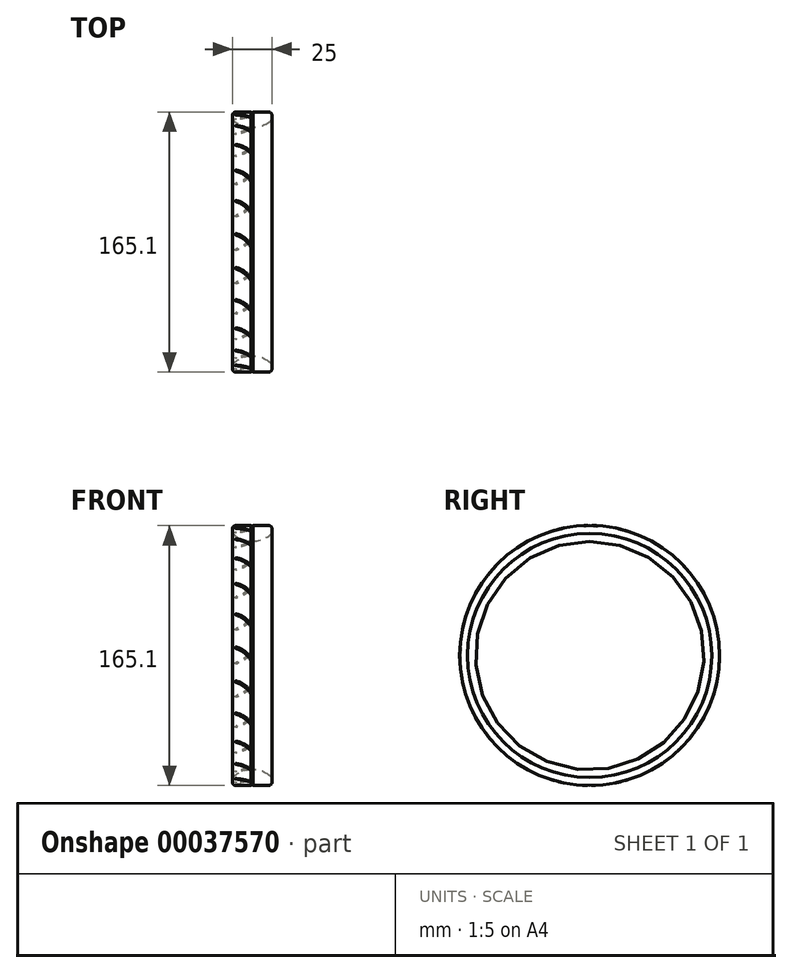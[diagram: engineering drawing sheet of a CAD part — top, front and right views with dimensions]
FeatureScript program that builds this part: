
annotation { "Feature Type Name" : "Feature", "Feature Type Description" : "" }
export const myFeature = defineFeature(function(context is Context, id is Id, definition is map)
    precondition{}
    {
        {
            var Q0;
            Q0=qCreatedBy(makeId("Top.planeOp"),FACE);
            var sketch = newSketch(context, id + "F0", { "sketchPlane" : qUnion([Q0])});
            skLineSegment(sketch, "E0", {"start": v(-134.1, 0) * mm, "end": v(143.87, 0) * mm, "construction": true});
            skLineSegment(sketch, "E1.left", {"start": v(-12.5, 80.55) * mm, "end": v(-12.5, 77.55) * mm});
            skLineSegment(sketch, "E1.right", {"start": v(12.5, 80.55) * mm, "end": v(12.5, 77.55) * mm});
            skArc(sketch, "E2", {"start": v(-12.5, 77.55) * mm, "mid": v(0, 72.59) * mm, "end": v(12.5, 77.55) * mm});
            skLineSegment(sketch, "E3", {"start": v(-10.5, 82.55) * mm, "end": v(-0.6, 82.55) * mm});
            skPoint(sketch, "E4.visualSharp", {"position": v(-12.5, 82.55) * mm});
            skArc(sketch, "E4.filletArc", {"start": v(-10.5, 82.55) * mm, "mid": v(-11.91, 81.96) * mm, "end": v(-12.5, 80.55) * mm});
            skPoint(sketch, "E5.visualSharp", {"position": v(12.5, 82.55) * mm});
            skArc(sketch, "E5.filletArc", {"start": v(12.5, 80.55) * mm, "mid": v(11.91, 81.96) * mm, "end": v(10.5, 82.55) * mm});
            skLineSegment(sketch, "E6.rect.bottom", {"start": v(0.6, 82.15) * mm, "end": v(-0.6, 82.15) * mm});
            skLineSegment(sketch, "E6.rect.left", {"start": v(0.6, 82.15) * mm, "end": v(0.6, 82.55) * mm});
            skLineSegment(sketch, "E6.rect.right", {"start": v(-0.6, 82.15) * mm, "end": v(-0.6, 82.55) * mm});
            skLineSegment(sketch, "E7.trimOffspring", {"start": v(0.6, 82.55) * mm, "end": v(10.5, 82.55) * mm});
            skSolve(sketch);
        }
        {
            var Q0;
            Q0=makeQuery(id+"F0.imprint","IMPRINT",FACE,{"disambiguationData":[TD([[makeQuery(id+"F0.imprint","IMPRINT",EDGE,{"derivedFrom":sQuery(id+"F0.wireOp",EDGE,"E1.left")}),1.0]])]});
            var Q1;
            Q1=sQuery(id+"F0.wireOp",EDGE,"E0");
            revolve(context, id + "F1", {"entities" : qUnion([Q0]), "axis" : qUnion([Q1]), "revolveType" : RevolveType.FULL});
        }
        {
            var Q0;
            Q0=qCreatedBy(makeId("Top.planeOp"),FACE);
            cPlane(context, id + "F2", {"entities" : qUnion([Q0]), "cplaneType" : CPlaneType.OFFSET, "offset" : 89.1 * mm, "width" : 150 * mm, "height" : 150 * mm});
        }
        {
            var Q0;
            Q0=qCreatedBy(makeId("Top.planeOp"),FACE);
            var sketch = newSketch(context, id + "F3", { "sketchPlane" : qUnion([Q0])});
            skLineSegment(sketch, "E8", {"start": v(-88.22, 0) * mm, "end": v(82.6, 0) * mm, "construction": true});
            skSolve(sketch);
        }
        {
            var Q0;
            Q0=qCreatedBy(id+"F2.planeOp",FACE);
            var sketch = newSketch(context, id + "F4", { "sketchPlane" : qUnion([Q0])});
            skArc(sketch, "E9", {"start": v(0, -5.08) * mm, "mid": v(-3.64, 1.64) * mm, "end": v(-10.3, 5.36) * mm});
            skArc(sketch, "E10", {"start": v(0, -5.08) * mm, "mid": v(-4.05, 0.87) * mm, "end": v(-10.3, 4.43) * mm});
            skArc(sketch, "E11", {"start": v(-10.3, 5.36) * mm, "mid": v(-10.68, 4.9) * mm, "end": v(-10.3, 4.43) * mm});
            skArc(sketch, "E12.MirrorCS", {"start": v(0, -5.08) * mm, "mid": v(3.64, 1.64) * mm, "end": v(10.3, 5.36) * mm});
            skArc(sketch, "E13.MirrorCS", {"start": v(0, -5.08) * mm, "mid": v(4.05, 0.87) * mm, "end": v(10.3, 4.43) * mm});
            skArc(sketch, "E14.MirrorCS", {"start": v(10.3, 5.36) * mm, "mid": v(10.68, 4.9) * mm, "end": v(10.3, 4.43) * mm});
            skSolve(sketch);
        }
        {
            var Q0;
            Q0=makeQuery(id+"F4.imprint","IMPRINT",FACE,{"disambiguationData":[TD([[makeQuery(id+"F4.imprint","IMPRINT",EDGE,{"derivedFrom":sQuery(id+"F4.wireOp",EDGE,"E9")}),1.0]])]});
            var Q1;
            Q1=makeQuery(id+"F4.imprint","IMPRINT",FACE,{"disambiguationData":[TD([[makeQuery(id+"F4.imprint","IMPRINT",EDGE,{"derivedFrom":sQuery(id+"F4.wireOp",EDGE,"E12.MirrorCS")}),-1.0]])]});
            var Q2;
            Q2=makeQuery(id+"F1.opRevolve","SWEPT_FACE",FACE,{"disambiguationData":[OSD([sQuery(id+"F0.wireOp",EDGE,"E6.rect.bottom")])]});
            extrude(context, id + "F5", {"entities" : qUnion([Q0, Q1]), "operationType" : NewBodyOperationType.REMOVE, "endBound" : BoundingType.UP_TO_SURFACE, "oppositeDirection" : true, "endBoundEntityFace" : qUnion([Q2]), "depth" : 1 * mm});
        }
        {
            var Q0;
            Q0=makeQuery(id+"F5.boolean.opBoolean","COPY",FACE,{"derivedFrom":makeQuery(id+"F5.opExtrude","SWEPT_FACE",FACE,{"disambiguationData":[OSD([sQuery(id+"F4.wireOp",EDGE,"E9")])]})});
            var Q1;
            Q1=makeQuery(id+"F5.boolean.opBoolean","COPY",FACE,{"derivedFrom":makeQuery(id+"F5.opExtrude","SWEPT_FACE",FACE,{"disambiguationData":[OSD([sQuery(id+"F4.wireOp",EDGE,"E11")])]})});
            var Q2;
            Q2=makeQuery(id+"F5.boolean.opBoolean","COPY",FACE,{"derivedFrom":makeQuery(id+"F5.opExtrude","SWEPT_FACE",FACE,{"disambiguationData":[OSD([sQuery(id+"F4.wireOp",EDGE,"E12.MirrorCS")])]})});
            var Q3;
            Q3=makeQuery(id+"F5.boolean.opBoolean","COPY",FACE,{"derivedFrom":makeQuery(id+"F5.opExtrude","SWEPT_FACE",FACE,{"disambiguationData":[OSD([sQuery(id+"F4.wireOp",EDGE,"E10")])]})});
            var Q4;
            Q4=makeQuery(id+"F5.boolean.opBoolean","COPY",FACE,{"derivedFrom":makeQuery(id+"F5.opExtrude","SWEPT_FACE",FACE,{"disambiguationData":[OSD([sQuery(id+"F4.wireOp",EDGE,"E13.MirrorCS")])]})});
            var Q5;
            Q5=makeQuery(id+"F5.boolean.opBoolean","COPY",FACE,{"derivedFrom":makeQuery(id+"F5.opExtrude","SWEPT_FACE",FACE,{"disambiguationData":[OSD([sQuery(id+"F4.wireOp",EDGE,"E14.MirrorCS")])]})});
            var Q6;
            Q6=sQuery(id+"F3.wireOp",EDGE,"E8");
            circularPattern(context, id + "F6", {"faces" : qUnion([Q0, Q1, Q2, Q3, Q4, Q5]), "axis" : qUnion([Q6]), "angle" : 360 * degree, "instanceCount" : round(24), "equalSpace" : true, "patternType" : PatternType.FACE});
        }
    });
